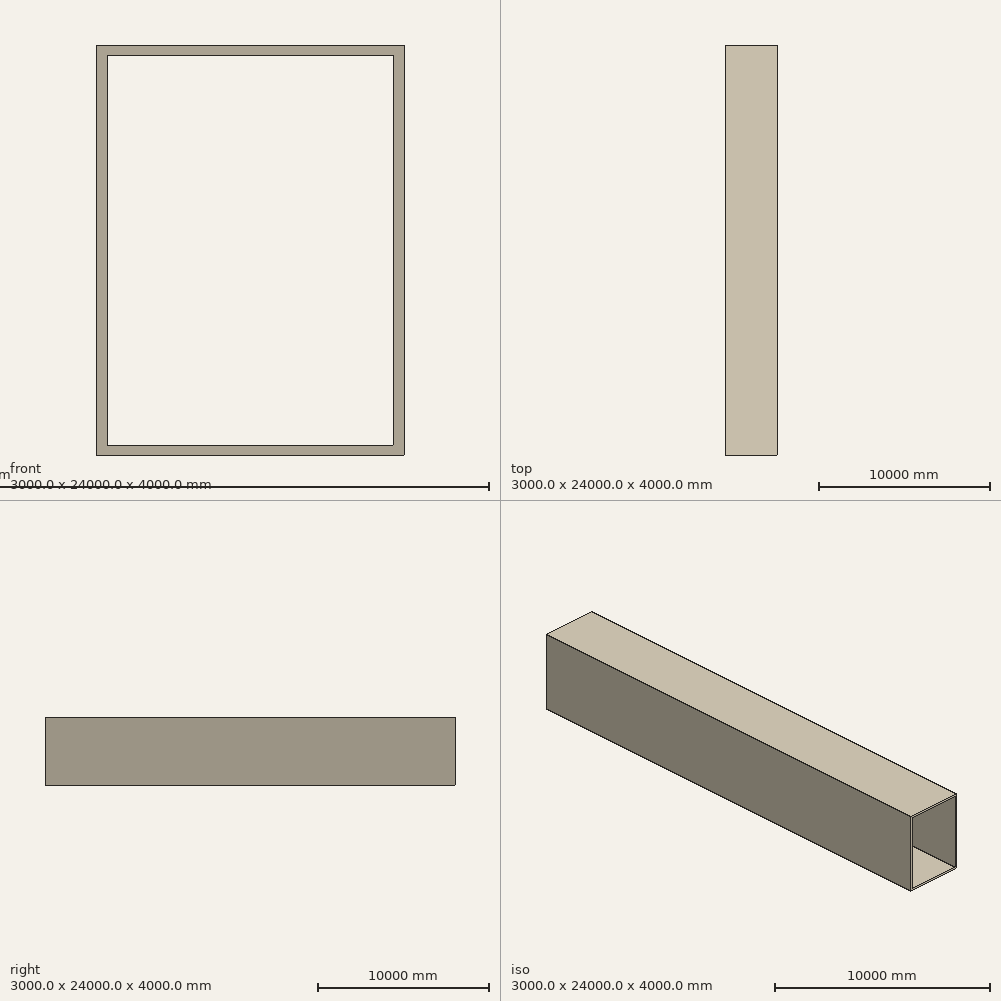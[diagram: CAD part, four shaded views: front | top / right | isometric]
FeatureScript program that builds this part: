
annotation { "Feature Type Name" : "Feature", "Feature Type Description" : "" }
export const myFeature = defineFeature(function(context is Context, id is Id, definition is map)
    precondition{}
    {
        {
            var Q0;
            Q0=qCreatedBy(makeId("Front.planeOp"),FACE);
            var sketch = newSketch(context, id + "F0", { "sketchPlane" : qUnion([Q0])});
            skLineSegment(sketch, "E0.bottom", {"start": v(0, 0) * mm, "end": v(2800, 0) * mm});
            skLineSegment(sketch, "E0.top", {"start": v(0, 3800) * mm, "end": v(2800, 3800) * mm});
            skLineSegment(sketch, "E0.left", {"start": v(0, 0) * mm, "end": v(0, 3800) * mm});
            skLineSegment(sketch, "E0.right", {"start": v(2800, 0) * mm, "end": v(2800, 3800) * mm});
            skLineSegment(sketch, "E1.bottom", {"start": v(-100, -100) * mm, "end": v(2900, -100) * mm});
            skLineSegment(sketch, "E1.top", {"start": v(-100, 3900) * mm, "end": v(2900, 3900) * mm});
            skLineSegment(sketch, "E1.left", {"start": v(-100, -100) * mm, "end": v(-100, 3900) * mm});
            skLineSegment(sketch, "E1.right", {"start": v(2900, -100) * mm, "end": v(2900, 3900) * mm});
            skSolve(sketch);
        }
        {
            var Q0;
            Q0=makeQuery(id+"F0.imprint","IMPRINT",FACE,{"disambiguationData":[TD([[makeQuery(id+"F0.imprint","IMPRINT",EDGE,{"derivedFrom":sQuery(id+"F0.wireOp",EDGE,"E0.bottom")}),-1.0]])]});
            extrude(context, id + "F1", {"entities" : qUnion([Q0]), "depth" : 24000 * mm, "offsetDistance" : 25 * mm});
        }
    });
